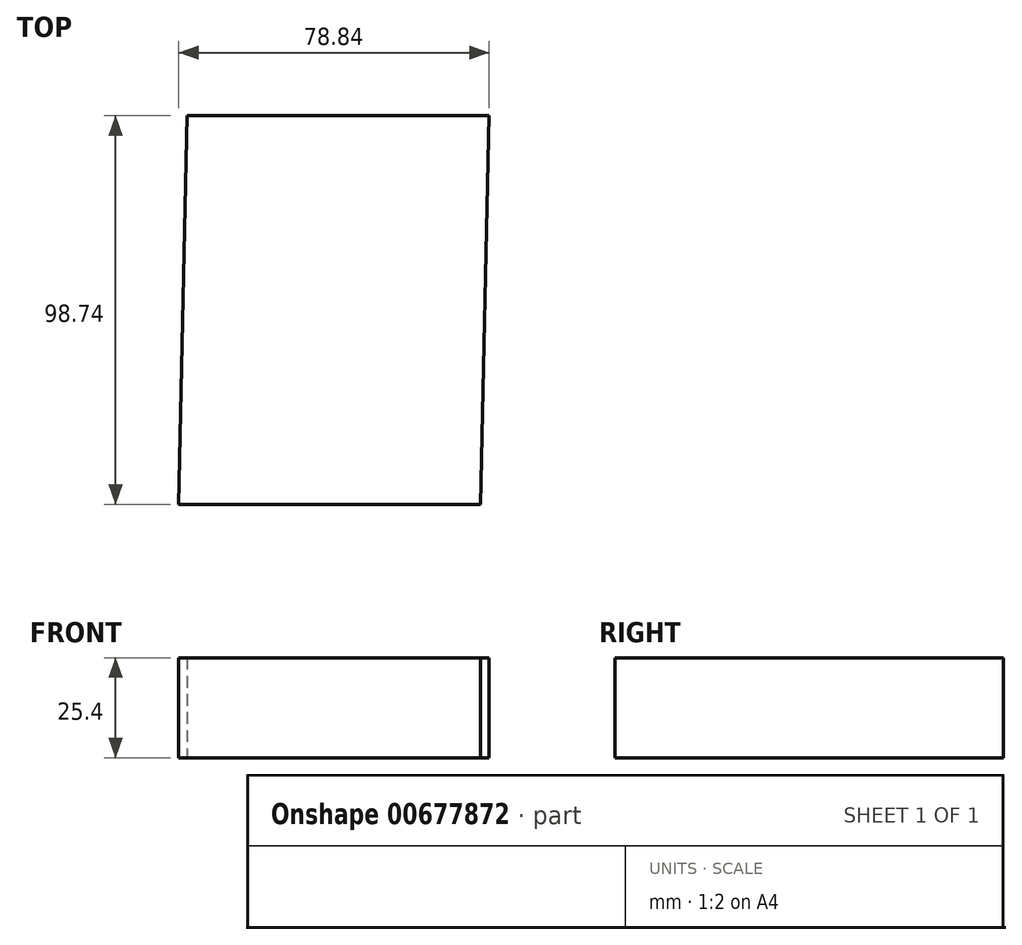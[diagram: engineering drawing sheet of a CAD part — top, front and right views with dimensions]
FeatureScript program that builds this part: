
annotation { "Feature Type Name" : "Feature", "Feature Type Description" : "" }
export const myFeature = defineFeature(function(context is Context, id is Id, definition is map)
    precondition{}
    {
        {
            var Q0;
            Q0=qCreatedBy(makeId("Top.planeOp"),FACE);
            var sketch = newSketch(context, id + "F0", { "sketchPlane" : qUnion([Q0])});
            skLineSegment(sketch, "E0.bottom", {"start": v(39.42, 49.37) * mm, "end": v(-37.28, 49.37) * mm});
            skLineSegment(sketch, "E0.top", {"start": v(37.28, -49.37) * mm, "end": v(-39.42, -49.37) * mm});
            skLineSegment(sketch, "E0.left", {"start": v(39.42, 49.37) * mm, "end": v(37.28, -49.37) * mm});
            skLineSegment(sketch, "E0.right", {"start": v(-37.28, 49.37) * mm, "end": v(-39.42, -49.37) * mm});
            skPoint(sketch, "E0.middle", {"position": v(0, 0) * mm});
            skSolve(sketch);
        }
        {
            var Q0;
            Q0=makeQuery(id+"F0.imprint","IMPRINT",FACE,{"disambiguationData":[TD([[makeQuery(id+"F0.imprint","IMPRINT",EDGE,{"derivedFrom":sQuery(id+"F0.wireOp",EDGE,"E0.bottom")}),1.0]])]});
            extrude(context, id + "F1", {"entities" : qUnion([Q0]), "depth" : 25.4 * mm, "offsetDistance" : 25.4 * mm});
        }
    });
